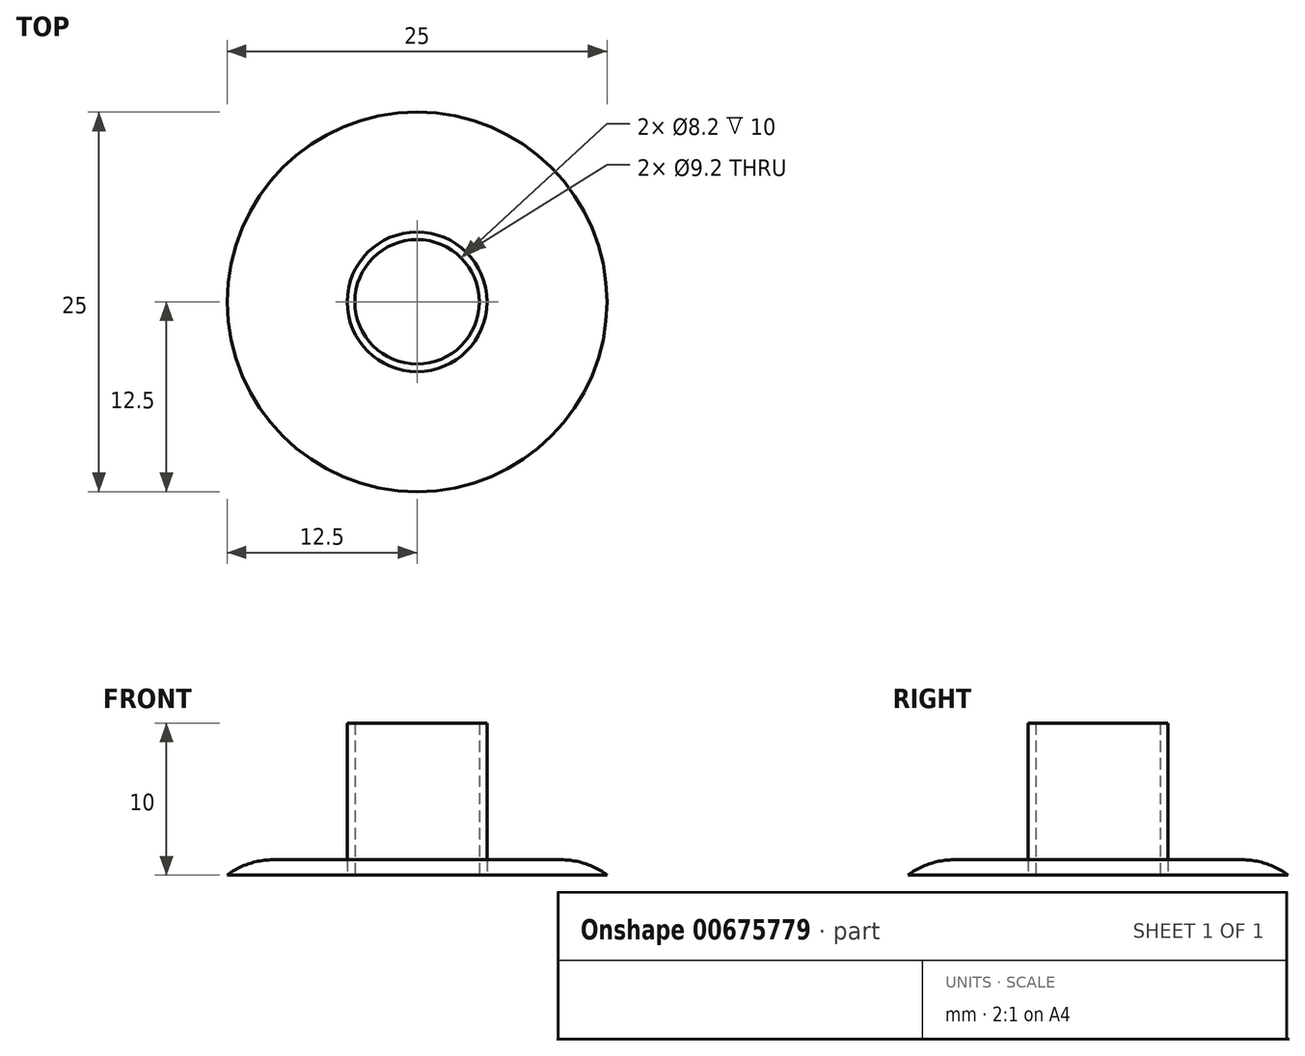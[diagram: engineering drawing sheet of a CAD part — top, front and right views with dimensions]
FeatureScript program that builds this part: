
annotation { "Feature Type Name" : "Feature", "Feature Type Description" : "" }
export const myFeature = defineFeature(function(context is Context, id is Id, definition is map)
    precondition{}
    {
        {
            var Q0;
            Q0=qCreatedBy(makeId("Top.planeOp"),FACE);
            var sketch = newSketch(context, id + "F0", { "sketchPlane" : qUnion([Q0])});
            skCircle(sketch, "E0", {"center": v(0, 0) * mm, "radius": 4.1 * mm});
            skCircle(sketch, "E1", {"center": v(0, 0) * mm, "radius": 12.5 * mm});
            skCircle(sketch, "E2", {"center": v(0, 0) * mm, "radius": 4.6 * mm});
            skSolve(sketch);
        }
        {
            var Q0;
            Q0=makeQuery(id+"F0.imprint","IMPRINT",FACE,{"disambiguationData":[TD([[makeQuery(id+"F0.imprint","IMPRINT",EDGE,{"derivedFrom":sQuery(id+"F0.wireOp",EDGE,"E0")}),-1.0]])]});
            extrude(context, id + "F1", {"entities" : qUnion([Q0]), "depth" : 10 * mm, "offsetDistance" : 25 * mm});
        }
        {
            var Q0;
            Q0 = qSketchRegion(id + "F0", true);
            extrude(context, id + "F2", {"entities" : qUnion([Q0]), "depth" : 1 * mm, "offsetDistance" : 25 * mm});
        }
        {
            var Q0;
            Q0=makeQuery(id+"F2.opExtrude","CAP_EDGE",EDGE,{"disambiguationData":[OSD([sQuery(id+"F0.wireOp",EDGE,"E1")])],"isStart":false});
            fillet(context, id + "F3", {"entities" : qUnion([Q0]), "radius" : 5 * mm, "tangentPropagation" : true, "allowEdgeOverflow" : false});
        }
    });
